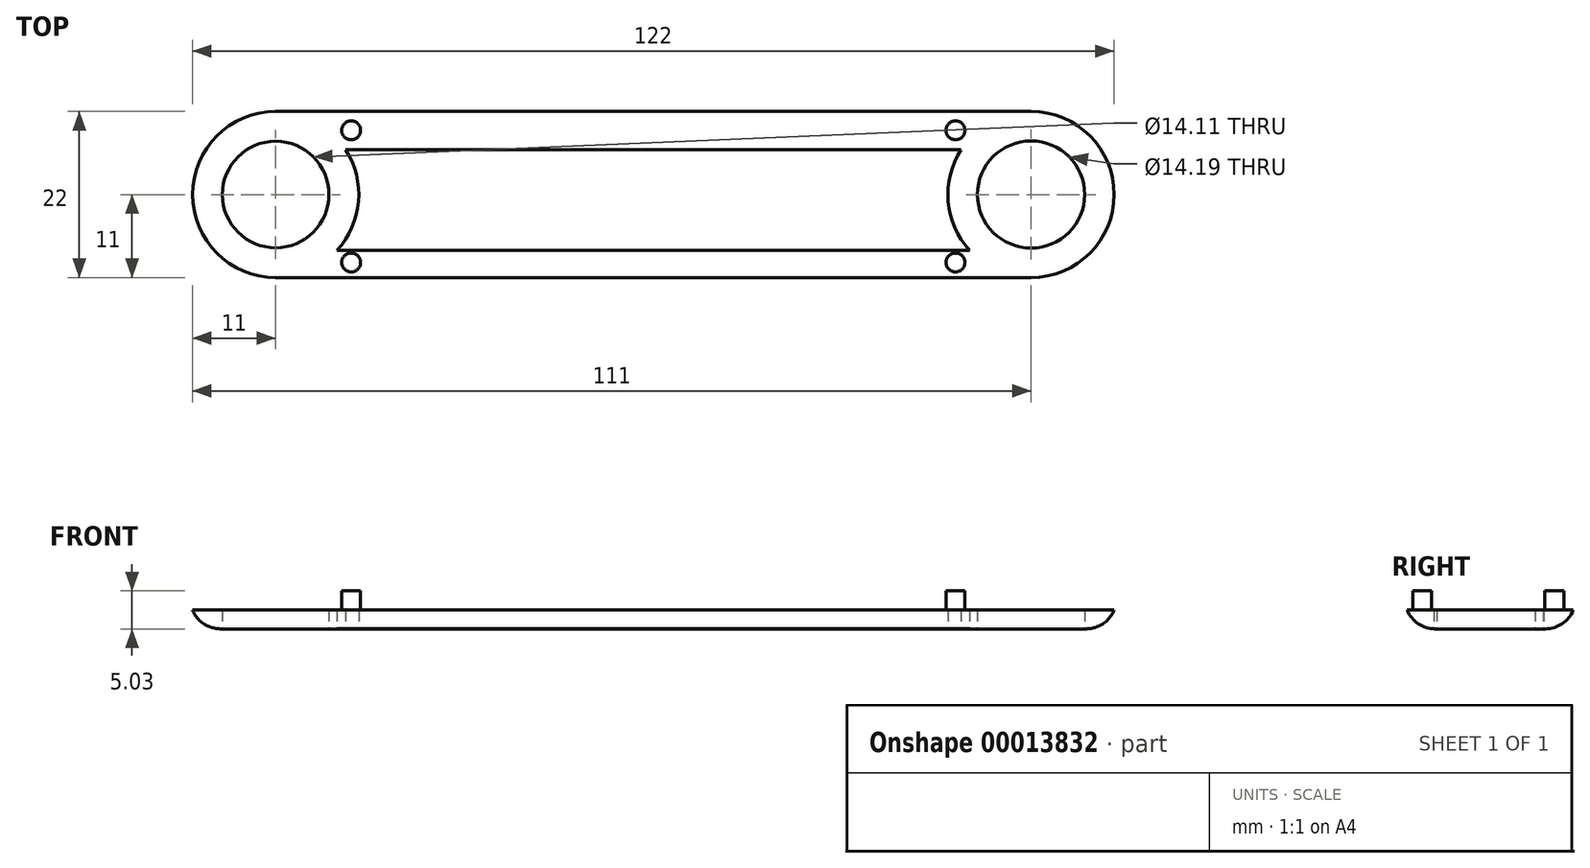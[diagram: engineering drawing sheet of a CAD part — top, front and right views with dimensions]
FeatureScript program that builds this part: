
annotation { "Feature Type Name" : "Feature", "Feature Type Description" : "" }
export const myFeature = defineFeature(function(context is Context, id is Id, definition is map)
    precondition{}
    {
        {
            var Q0;
            Q0=qCreatedBy(makeId("Top.planeOp"),FACE);
            var sketch = newSketch(context, id + "F0", { "sketchPlane" : qUnion([Q0])});
            skCircle(sketch, "E0", {"center": v(-50, 0) * mm, "radius": 7.05 * mm});
            skCircle(sketch, "E1", {"center": v(50, 0) * mm, "radius": 7.1 * mm});
            skArc(sketch, "E2", {"start": v(-41.88, -7.42) * mm, "mid": v(-39.04, -0.93) * mm, "end": v(-40.75, 5.95) * mm});
            skArc(sketch, "E3", {"start": v(50, -11) * mm, "mid": v(61, 0) * mm, "end": v(50, 11) * mm});
            skLineSegment(sketch, "E4.bottom", {"start": v(-50, -11) * mm, "end": v(50, -11) * mm});
            skLineSegment(sketch, "E4.top", {"start": v(-50, 11) * mm, "end": v(50, 11) * mm});
            skLineSegment(sketch, "E5.bottom", {"start": v(-41.88, -7.42) * mm, "end": v(41.88, -7.42) * mm});
            skLineSegment(sketch, "E5.top", {"start": v(-40.75, 5.95) * mm, "end": v(40.75, 5.95) * mm});
            skArc(sketch, "E6.trimOffspring", {"start": v(-50, 11) * mm, "mid": v(-61, 0) * mm, "end": v(-50, -11) * mm});
            skArc(sketch, "E7.trimOffspring", {"start": v(40.75, 5.95) * mm, "mid": v(39.04, -0.93) * mm, "end": v(41.88, -7.42) * mm});
            skSolve(sketch);
        }
        {
            var Q0;
            Q0=makeQuery(id+"F0.imprint","IMPRINT",FACE,{"disambiguationData":[TD([[makeQuery(id+"F0.imprint","IMPRINT",EDGE,{"derivedFrom":sQuery(id+"F0.wireOp",EDGE,"E0")}),-1.0]])]});
            extrude(context, id + "F1", {"entities" : qUnion([Q0]), "depth" : 2.5 * mm});
        }
        {
            var Q0;
            Q0=makeQuery(id+"F1.opExtrude","CAP_FACE",FACE,{"disambiguationData":[OSD([sQuery(id+"F0.wireOp",EDGE,"E0"),sQuery(id+"F0.wireOp",EDGE,"E1"),sQuery(id+"F0.wireOp",EDGE,"E2"),sQuery(id+"F0.wireOp",EDGE,"E3"),sQuery(id+"F0.wireOp",EDGE,"E4.bottom"),sQuery(id+"F0.wireOp",EDGE,"E4.top"),sQuery(id+"F0.wireOp",EDGE,"E5.bottom"),sQuery(id+"F0.wireOp",EDGE,"E5.top"),sQuery(id+"F0.wireOp",EDGE,"E6.trimOffspring"),sQuery(id+"F0.wireOp",EDGE,"E7.trimOffspring")])],"isStart":false});
            var sketch = newSketch(context, id + "F2", { "sketchPlane" : qUnion([Q0])});
            skCircle(sketch, "E8", {"center": v(-40, 8.5) * mm, "radius": 1.25 * mm});
            skCircle(sketch, "E9", {"center": v(-40, -9) * mm, "radius": 1.25 * mm});
            skCircle(sketch, "E10", {"center": v(40, -9) * mm, "radius": 1.25 * mm});
            skCircle(sketch, "E11", {"center": v(40, 8.5) * mm, "radius": 1.25 * mm});
            skSolve(sketch);
        }
        {
            var Q0;
            Q0 = qSketchRegion(id + "F2", true);
            extrude(context, id + "F3", {"entities" : qUnion([Q0]), "operationType" : NewBodyOperationType.ADD, "depth" : 2.52 * mm});
        }
        {
            var Q0;
            Q0=makeQuery(id+"F1.opExtrude","CAP_EDGE",EDGE,{"disambiguationData":[OSD([sQuery(id+"F0.wireOp",EDGE,"E4.bottom")])],"isStart":true});
            fillet(context, id + "F4", {"entities" : qUnion([Q0]), "radius" : 4 * mm, "tangentPropagation" : true, "allowEdgeOverflow" : false});
        }
    });
